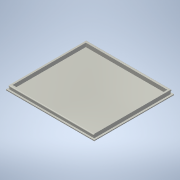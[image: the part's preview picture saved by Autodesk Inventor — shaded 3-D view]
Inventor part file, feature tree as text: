
AUTODESK INVENTOR PART (.ipt)
format: ipt  version: 2022.3 (Build 263350000, 350)  size: 147,456 bytes
history: native  units: mm
features: other x4, extrude x3, sketch x2, projected_geometry x2, folder x1, pattern_circular x1
ambient origin geometry x8: Origin, YZ Plane, XZ Plane, XY Plane, X Axis, Y Axis, Z Axis, Center Point
bodies: Body1 (feature_tree)
feature tree (13):
  other  "BARB_bottom"
  folder  "Master_XZ"
  extrude  "Floor"  Depth=2.0mm
  extrude  "Walls"  Depth=6.0mm TaperAngle=0.0deg
  other  "Lip_profile"
  extrude  "Lip"  Depth=2.0mm
  other  "Lip_edge_right"
  other  "Lip_edge_left"
  pattern_circular  "Circular Pattern1"  [2 undecoded]
  sketch  "Sketch3"  dims[d0=2.0mm d1=2.0mm]
  projected_geometry  "Projected Loop1"
  sketch  "Sketch4"  dims[d2=2.0mm d3=0.0mm d4=6.0mm d5=0.0mm d6=2.0mm d7=1.0mm d8=100.0mm d9=0.0mm d10=105.0mm d12=20.0mm d13=360.0deg d15=95.0mm d16=90.0deg d17=90.0deg]
  projected_geometry  "Projected Loop2"
note: 2 required parameter values undecoded (feature->parameter linkage not recoverable at this tier; creation-order binding heuristic only, values carry confidence <= 0.55)
